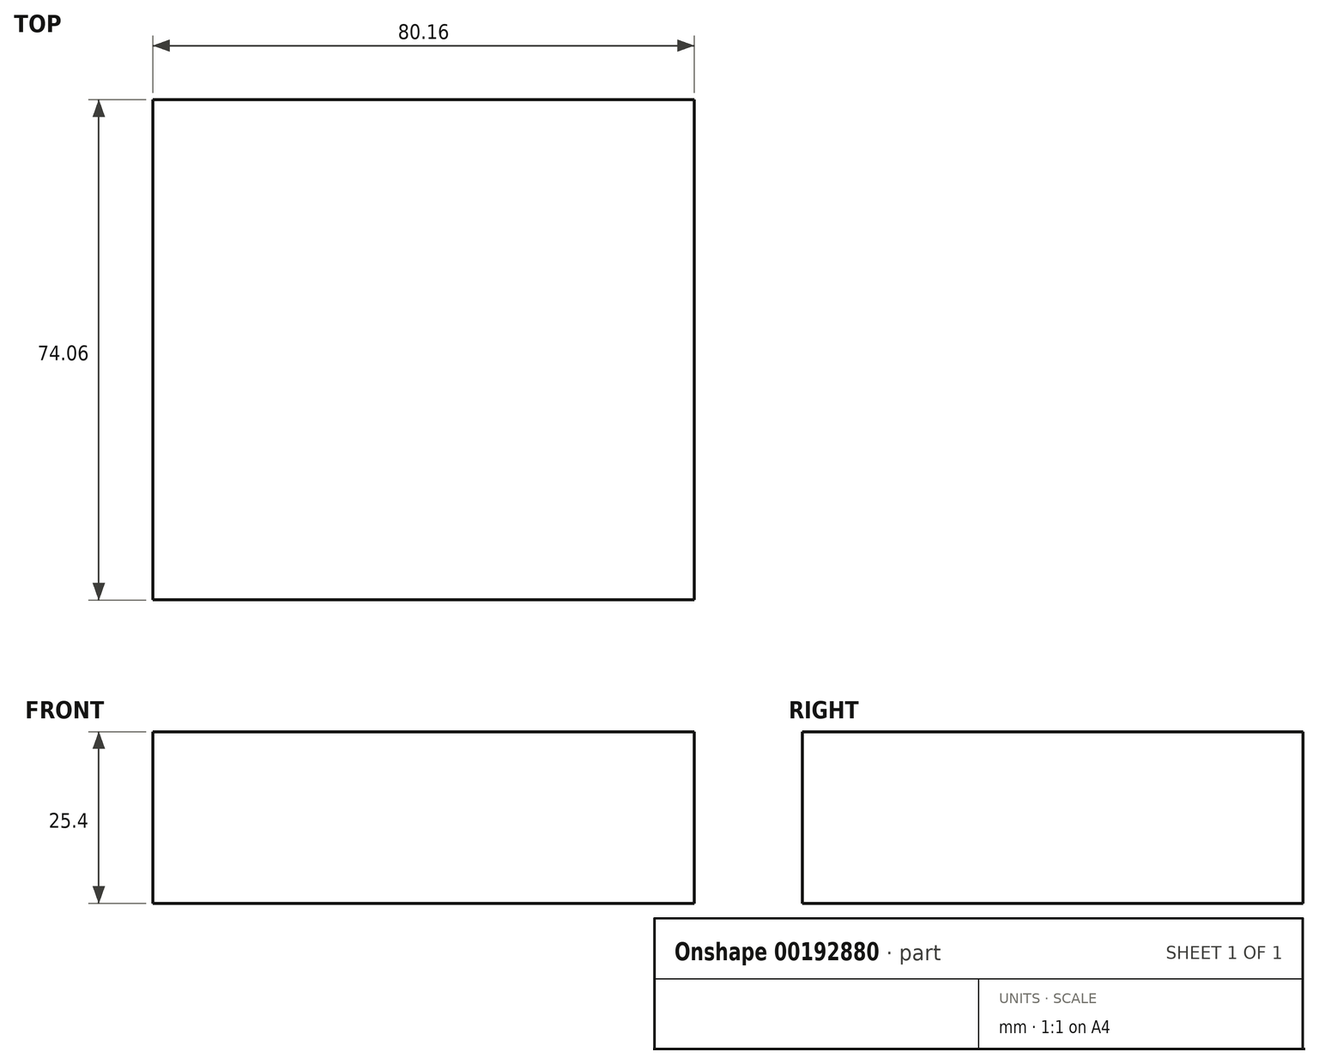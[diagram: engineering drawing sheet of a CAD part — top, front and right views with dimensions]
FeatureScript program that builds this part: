
annotation { "Feature Type Name" : "Feature", "Feature Type Description" : "" }
export const myFeature = defineFeature(function(context is Context, id is Id, definition is map)
    precondition{}
    {
        {
            var Q0;
            Q0=qCreatedBy(makeId("Top.planeOp"),FACE);
            var sketch = newSketch(context, id + "F0", { "sketchPlane" : qUnion([Q0])});
            skLineSegment(sketch, "E0.bottom", {"start": v(40.08, 37.03) * mm, "end": v(-40.08, 37.03) * mm});
            skLineSegment(sketch, "E0.top", {"start": v(40.08, -37.03) * mm, "end": v(-40.08, -37.03) * mm});
            skLineSegment(sketch, "E0.left", {"start": v(40.08, 37.03) * mm, "end": v(40.08, -37.03) * mm});
            skLineSegment(sketch, "E0.right", {"start": v(-40.08, 37.03) * mm, "end": v(-40.08, -37.03) * mm});
            skPoint(sketch, "E0.middle", {"position": v(0, 0) * mm});
            skSolve(sketch);
        }
        {
            var Q0;
            Q0=makeQuery(id+"F0.imprint","IMPRINT",FACE,{"disambiguationData":[TD([[makeQuery(id+"F0.imprint","IMPRINT",EDGE,{"derivedFrom":sQuery(id+"F0.wireOp",EDGE,"E0.bottom")}),1.0]])]});
            extrude(context, id + "F1", {"entities" : qUnion([Q0]), "depth" : 25.4 * mm});
        }
    });
